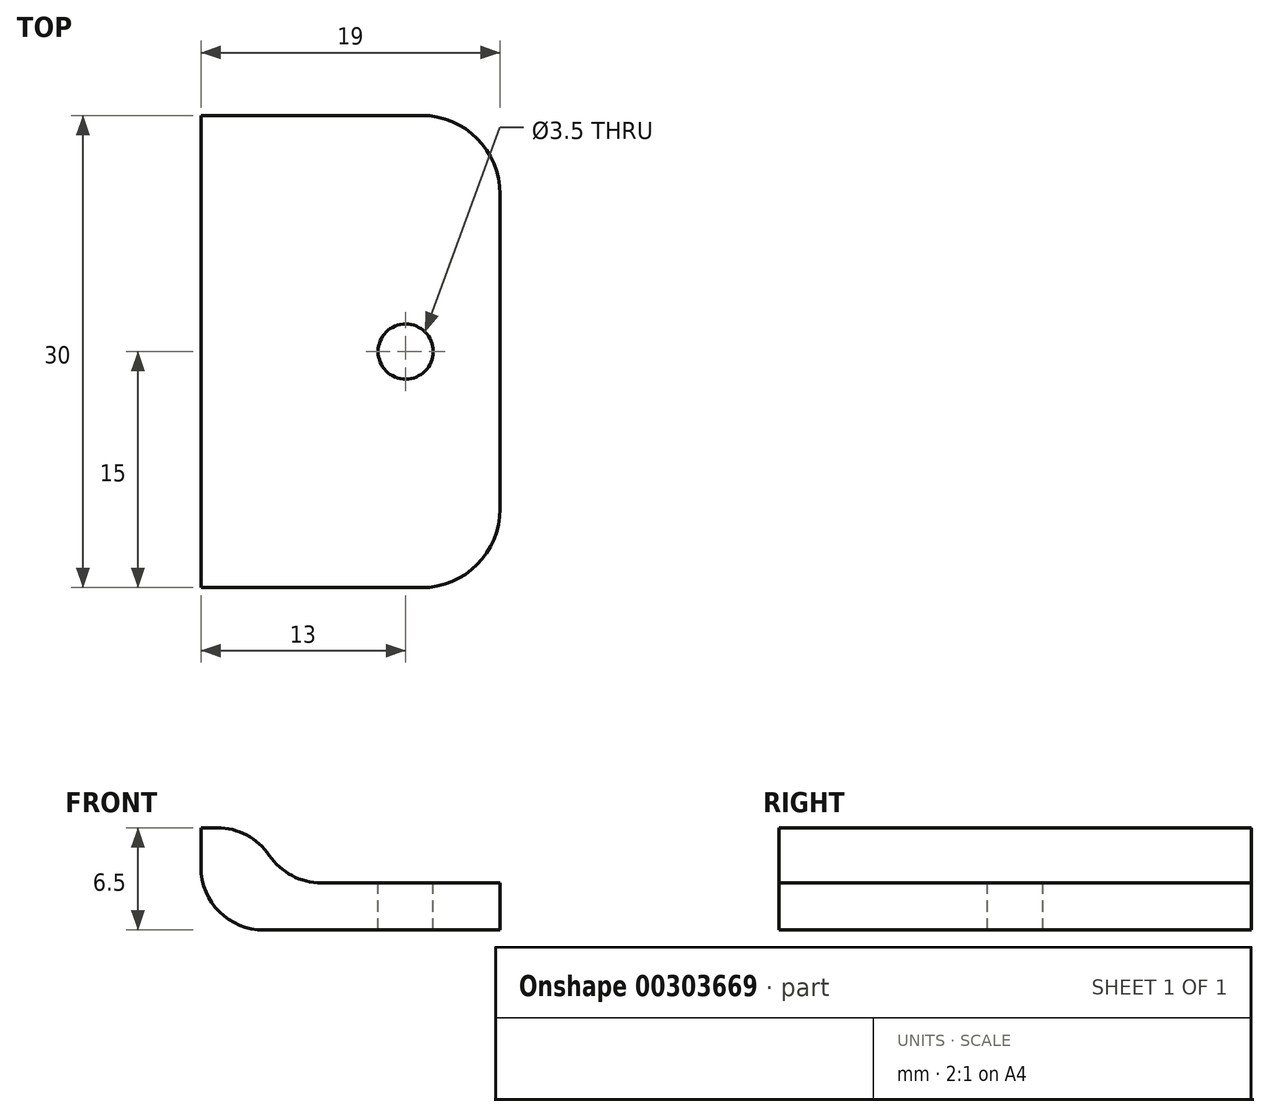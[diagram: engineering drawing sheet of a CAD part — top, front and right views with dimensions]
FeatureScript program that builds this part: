
annotation { "Feature Type Name" : "Feature", "Feature Type Description" : "" }
export const myFeature = defineFeature(function(context is Context, id is Id, definition is map)
    precondition{}
    {
        {
            var Q0;
            Q0=qCreatedBy(makeId("Top.planeOp"),FACE);
            var sketch = newSketch(context, id + "F0", { "sketchPlane" : qUnion([Q0])});
            skLineSegment(sketch, "E0.bottom", {"start": v(-19.5, 15) * mm, "end": v(2.5, 15) * mm});
            skLineSegment(sketch, "E0.top", {"start": v(-19.5, -15) * mm, "end": v(2.5, -15) * mm});
            skLineSegment(sketch, "E0.left", {"start": v(-19.5, 15) * mm, "end": v(-19.5, -15) * mm});
            skLineSegment(sketch, "E0.right", {"start": v(2.5, 15) * mm, "end": v(2.5, -15) * mm});
            skLineSegment(sketch, "E1", {"start": v(-31.73, 0) * mm, "end": v(31.45, 0) * mm, "construction": true});
            skLineSegment(sketch, "E2", {"start": v(-14.5, 19.74) * mm, "end": v(-14.5, -20.6) * mm, "construction": true});
            skCircle(sketch, "E3", {"center": v(-14.5, 7.5) * mm, "radius": 1.75 * mm});
            skCircle(sketch, "E4", {"center": v(-14.5, -7.5) * mm, "radius": 1.75 * mm});
            skLineSegment(sketch, "E5.bottom", {"start": v(11.5, 15) * mm, "end": v(-2.5, 15) * mm});
            skLineSegment(sketch, "E5.top", {"start": v(11.5, -15) * mm, "end": v(-2.5, -15) * mm});
            skLineSegment(sketch, "E5.left", {"start": v(16.5, 10) * mm, "end": v(16.5, -10) * mm});
            skLineSegment(sketch, "E5.right", {"start": v(-2.5, 15) * mm, "end": v(-2.5, -15) * mm});
            skLineSegment(sketch, "E6", {"start": v(10.5, 19.74) * mm, "end": v(10.5, -20.6) * mm, "construction": true});
            skCircle(sketch, "E7", {"center": v(10.5, 0) * mm, "radius": 1.75 * mm});
            skPoint(sketch, "E8.visualSharp", {"position": v(16.5, -15) * mm});
            skArc(sketch, "E8.filletArc", {"start": v(11.5, -15) * mm, "mid": v(15.04, -13.54) * mm, "end": v(16.5, -10) * mm});
            skPoint(sketch, "E9.visualSharp", {"position": v(16.5, 15) * mm});
            skArc(sketch, "E9.filletArc", {"start": v(16.5, 10) * mm, "mid": v(15.04, 13.54) * mm, "end": v(11.5, 15) * mm});
            skLineSegment(sketch, "E10", {"start": v(0, 22.12) * mm, "end": v(0, -22.25) * mm, "construction": true});
            skSolve(sketch);
        }
        {
            var Q0;
            {var subQ0=sQuery(id+"F0.wireOp",EDGE,"E0.right");Q0=makeQuery(id+"F0.imprint","IMPRINT",FACE,{"disambiguationData":[TD([[makeQuery(id+"F0.imprint","IMPRINT",EDGE,{"derivedFrom":subQ0}),-1.0]])]});}
            var Q1;
            Q1=makeQuery(id+"F0.imprint","IMPRINT",FACE,{"disambiguationData":[TD([[makeQuery(id+"F0.imprint","IMPRINT",EDGE,{"derivedFrom":sQuery(id+"F0.wireOp",EDGE,"E0.bottom")}),-1.0]])]});
            extrude(context, id + "F1", {"entities" : qUnion([Q0, Q1]), "depth" : 3.5 * mm});
        }
        {
            var Q0;
            {var subQ2=sQuery(id+"F0.wireOp",EDGE,"E0.right");Q0=makeQuery(id+"F0.imprint","IMPRINT",FACE,{"disambiguationData":[TD([[makeQuery(id+"F0.imprint","IMPRINT",EDGE,{"derivedFrom":subQ2}),1.0]])]});}
            var Q1;
            {var subQ0=sQuery(id+"F0.wireOp",EDGE,"E0.right");Q1=makeQuery(id+"F0.imprint","IMPRINT",FACE,{"disambiguationData":[TD([[makeQuery(id+"F0.imprint","IMPRINT",EDGE,{"derivedFrom":subQ0}),-1.0]])]});}
            var Q2;
            Q2=sQuery(id+"F0.wireOp",EDGE,"E5.right");
            var Q3;
            Q3=sQuery(id+"F0.wireOp",EDGE,"E5.bottom");
            var Q4;
            Q4=sQuery(id+"F0.wireOp",EDGE,"E5.left");
            var Q5;
            Q5=sQuery(id+"F0.wireOp",EDGE,"E5.top");
            extrude(context, id + "F2", {"entities" : qUnion([Q0, Q1]), "operationType" : NewBodyOperationType.ADD, "surfaceEntities" : qUnion([Q2, Q3, Q4, Q5]), "oppositeDirection" : true, "depth" : 3 * mm});
        }
        {
            var Q0;
            Q0=makeQuery(id+"F1.opExtrude","CAP_EDGE",EDGE,{"disambiguationData":[OSD([sQuery(id+"F0.wireOp",EDGE,"E0.right")])],"isStart":false});
            var Q1;
            Q1=makeQuery(id+"F2.opExtrude","CAP_EDGE",EDGE,{"disambiguationData":[OSD([sQuery(id+"F0.wireOp",EDGE,"E5.right")])],"isStart":false});
            fillet(context, id + "F3", {"entities" : qUnion([Q0, Q1]), "radius" : 4 * mm, "tangentPropagation" : true, "allowEdgeOverflow" : false});
        }
        {
            var Q0;
            Q0=makeQuery(id+"F1.opExtrude","CAP_FACE",FACE,{"disambiguationData":[OSD([sQuery(id+"F0.wireOp",EDGE,"E0.bottom"),sQuery(id+"F0.wireOp",EDGE,"E0.top"),sQuery(id+"F0.wireOp",EDGE,"E0.left"),sQuery(id+"F0.wireOp",EDGE,"E0.right"),sQuery(id+"F0.wireOp",EDGE,"E3"),sQuery(id+"F0.wireOp",EDGE,"E4"),sQuery(id+"F0.wireOp",EDGE,"E5.bottom"),sQuery(id+"F0.wireOp",EDGE,"E5.top")])],"isStart":false});
            var sketch = newSketch(context, id + "F4", { "sketchPlane" : qUnion([Q0])});
            skCircle(sketch, "E11", {"center": v(-14.5, 7.5) * mm, "radius": 3.25 * mm});
            skCircle(sketch, "E12", {"center": v(-14.5, -7.5) * mm, "radius": 3.25 * mm});
            skSolve(sketch);
        }
        {
            var Q0;
            Q0 = qSketchRegion(id + "F4", true);
            extrude(context, id + "F5", {"entities" : qUnion([Q0]), "operationType" : NewBodyOperationType.REMOVE, "oppositeDirection" : true, "depth" : 1.5 * mm});
        }
        {
            var Q0;
            Q0=makeQuery(id+"F3.opFillet","BLEND_EDGE",EDGE,{"blendedFrom":[makeQuery(id+"F1.opExtrude","CAP_EDGE",EDGE,{"disambiguationData":[OSD([sQuery(id+"F0.wireOp",EDGE,"E0.right")])],"isStart":false}),makeQuery(id+"F2.opExtrude","CAP_FACE",FACE,{"disambiguationData":[OSD([sQuery(id+"F0.wireOp",EDGE,"E5.bottom"),sQuery(id+"F0.wireOp",EDGE,"E5.top"),sQuery(id+"F0.wireOp",EDGE,"E5.left"),sQuery(id+"F0.wireOp",EDGE,"E5.right"),sQuery(id+"F0.wireOp",EDGE,"E7"),sQuery(id+"F0.wireOp",EDGE,"E8.filletArc"),sQuery(id+"F0.wireOp",EDGE,"E9.filletArc")])],"isStart":true})],"blendedInto":[makeQuery(id+"F2.opExtrude","CAP_FACE",FACE,{"disambiguationData":[OSD([sQuery(id+"F0.wireOp",EDGE,"E5.bottom"),sQuery(id+"F0.wireOp",EDGE,"E5.top"),sQuery(id+"F0.wireOp",EDGE,"E5.left"),sQuery(id+"F0.wireOp",EDGE,"E5.right"),sQuery(id+"F0.wireOp",EDGE,"E7"),sQuery(id+"F0.wireOp",EDGE,"E8.filletArc"),sQuery(id+"F0.wireOp",EDGE,"E9.filletArc")])],"isStart":true})]});
            fillet(context, id + "F6", {"entities" : qUnion([Q0]), "radius" : 4 * mm, "tangentPropagation" : true, "allowEdgeOverflow" : false});
        }
    });
